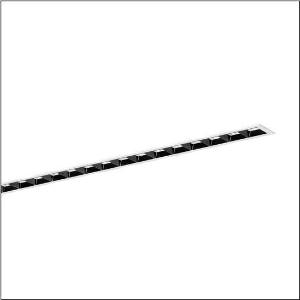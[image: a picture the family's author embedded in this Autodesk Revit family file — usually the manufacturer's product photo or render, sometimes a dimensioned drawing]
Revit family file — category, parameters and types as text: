
# Revit family: silica_r__21_51mx12dc4awb_60db
name_source: partatom
category: Lighting Fixtures
units: mm (PartAtom-declared; Revit-internal decimal feet)

## family parameters
Cut with Voids When Loaded = No
Host = Face
Light Source = No
Part Type = Normal
Room Calculation Point = No
Round Connector Dimension = Use Diameter
Shared = No

## types (1)
- --- (1 x LED, 10800 lm, 64.7 W, 4000K)
    Apparent Load = 65 VA
    CIE Flux Codes = 86 100 100 100 100
    Color Rendering = 80
    Color Temperature = 4000K
    Default Elevation = 1800 mm
    Description = Silica® 21, office luminaire, primary light control with darklight reflector, of PMMA, black, CAT 2 (L<= 3000cd/m²), light emission: direct distribution, primary light characteristic: symmetric, installation type: recessed, LED, rated luminous flux: 10.800lm, luminous efficacy: 167lm/W, light colour: 840, colour temperature: 4000K, with terminal, 3+2-pole, max. 2.5mm², mains connection: 220..240V, AC, 50/60Hz, rated input power: 64.7W, luminaire housing, of aluminium, traffic white (RAL 9016), length: 3.028mm, width: 79mm, height: 53mm, protection rating (complete): IP20, insulation class (complete): insulation class I (protective earthing), certification: CE, permissible operating ambient temperature: 0..+35°C, standard: EN 50419, packaging unit: 1 piece
    Height = 0 mm  [stored 0 ft]
    Lamp = 1 x LED
    Lamp Light Flux = 10800 lm
    Lamp Power = 64.7 W
    Lamp count = 1
    Length = 3027 mm
    Luminous efficacy = 167 lm/W
    Manufacturer = Siteco
    ModVariant = No
    Model = 51MX12DC4AWB
    Mounting Place = Ceiling
    Mounting Type = Recessed
    Number of Poles = 1
    OnlyDefault = Yes
    Power Factor = 1
    Product Name = Silica® 21
    Product group = office luminaire | ceiling recessed
    ProductGroupID = 401
    Protection Class = Protection class I
    Protection Degree = IP 20
    RLX_Detail_Level = 1
    RLX_Emergency_Light_Flux = 0 lm
    RLX_Emergency_Type = 0
    RLX_Emergency_Type_DB = No
    RlxData = <blob elided: 62681 chars, md5=7b0b20cb>
    Socket = socket
    Standby Power = 0 W
    System Light Flux = 10800 lm
    System Power = 65 W
    Type Comments = factory setting: luminous flux: 100 % | dim-lin: 254 | 366 mA
    Type Image = l_1297791.jpg
    URL = http://relux.com
    VarID = @adj_055577
    Voltage = 0 V
    Weight = 0.00 kg
    Width = 79 mm

note: [stored X ft] marks values corroborated as IEEE doubles in the binary element streams (Revit-internal decimal feet)

## geometry (parser evidence)
native form markers: Blend x4, Sweep x9
no freeform markers — native parametric forms only
